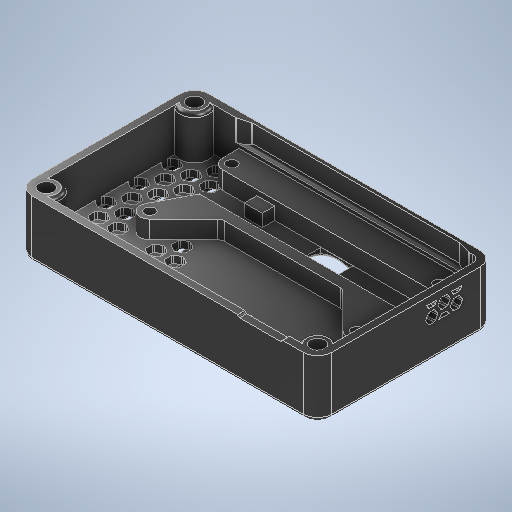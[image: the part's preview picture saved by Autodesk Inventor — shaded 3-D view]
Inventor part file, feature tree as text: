
AUTODESK INVENTOR PART (.ipt)
format: ipt  version: 2025 (Build 290162000, 162)  size: 2,251,264 bytes
history: native  units: mm
features: extrude x15, sketch x14, reference x9, fillet x8, projected_geometry x4, other x3, draft x1
ambient origin geometry x8: Origin, YZ Plane, XZ Plane, XY Plane, X Axis, Y Axis, Z Axis, Center Point
bodies: Solid1 (feature_tree)
feature tree (54):
  sketch  "Sketch1"  dims[d1=80.0mm d2=2.0mm]
  extrude  "Extrusion1"  Depth=2.0mm
  extrude  "Extrusion2"  Depth=5.5mm
  extrude  "Extrusion4"  Depth=9.1mm
  extrude  "Extrusion5"  Depth=2.0mm TaperAngle=0.0deg
  sketch  "Sketch2"  dims[d8=62.0mm d9=9.1mm]
  extrude  "Extrusion14"  Depth=12.0mm
  extrude  "Extrusion6"  Depth=5.0mm
  draft  "FaceDraft1"
  extrude  "Extrusion7"  Depth=13.0mm
  extrude  "Extrusion8"  Depth=4.0mm
  fillet  "Fillet6"  Radius=3.0mm
  fillet  "Fillet8"  Radius=2.0mm
  fillet  "Fillet9"  [1 undecoded]
  extrude  "Extrusion9"  Depth=5.0mm TaperAngle=0.0deg
  fillet  "Fillet10"  Radius=4.0mm
  extrude  "Extrusion11"  Depth=2.0mm
  fillet  "Fillet11"  Radius=2.0mm
  fillet  "Fillet12"  [1 undecoded]
  extrude  "Extrusion12"  Depth=2.0mm
  extrude  "Extrusion13"  TaperAngle=60.0deg  [1 undecoded]
  fillet  "Fillet13"  Radius=5.0mm
  extrude  "Extrusion15"  Depth=5.0mm
  fillet  "Fillet14"  Radius=7.0mm
  extrude  "Extrusion16"  Depth=8.0mm TaperAngle=0.0deg
  extrude  "Extrusion17"  Depth=0.5mm
  sketch  "Sketch Rectangular Pattern1"  dims[d3=2.0mm d4=2.9mm d5=58.0mm d6=23.0mm d7=5.5mm]
  projected_geometry  "Projected Loop2"
  sketch  "Sketch4"  dims[d10=9.0mm d11=2.0mm d12=0.0mm]
  sketch  "Sketch Rectangular Pattern6"  dims[d21=8.0mm d22=5.0mm]
  projected_geometry  "Projected Loop7"
  sketch  "Sketch5"  dims[d13=12.0mm d14=0.0mm d18=28.0mm]
  projected_geometry  "Projected Loop8"
  sketch  "Sketch Rectangular Pattern7"  dims[d32=2.0mm d33=4.0mm d34=3.0mm d35=2.0mm d36=135.0deg]
  sketch  "Sketch Rectangular Pattern8"  dims[d42=4.0mm d43=20.0mm d44=2.0mm d45=135.0deg]
  sketch  "Sketch Rectangular Pattern9"  dims[d51=2.0mm d52=0.0mm d54=60.0deg d55=5.0mm]
  sketch  "Sketch Rectangular Pattern10"  dims[d85=3.5mm d86=0.0mm d87=8.0mm d88=0.0mm d89=0.5mm d91=2.0mm d92=1.0mm d93=3.5mm d94=15.0mm d95=49.5mm d96=45.5mm d97=2.9mm d99=7.0mm d100=0.0mm d101=1.0mm d137=110.0mm d139=5.0mm d140=10.0mm d142=10.0mm d144=10.0mm d145=0.0mm d146=3.0mm d147=2.0mm d148=1.0mm d149=0.5mm d150=4.0mm d151=0.5mm d152=30.0mm d154=5.333333mm d155=10.0mm d157=10.0mm d159=40.0mm d161=5.333333mm d162=10.0mm d164=10.0mm d166=50.0mm d168=5.333333mm d169=10.0mm d171=10.0mm d173=90.0mm d175=5.333333mm d176=10.0mm d178=10.0mm d180=2.0mm d181=0.0mm d182=2.0mm d183=0.0mm d184=1.0mm d185=0.0mm d186=0.5mm d187=1.0mm d188=15.0deg d189=15.0deg d190=6.0mm d191=0.0mm d192=1.0mm d193=4.1mm d194=4.1mm d195=0.0mm d196=0.5mm d197=3.0mm d198=5.0mm d200=4.1mm d201=0.0mm d202=0.5mm d203=3.0mm d204=4.0mm d206=0.5mm d207=3.0mm d208=0.5mm d209=3.0mm d210=0.5mm d211=3.0mm d212=0.5mm d213=3.0mm d90=0.0mm]
  sketch  "Sketch6"  dims[d23=50.0mm d25=6.0mm d26=10.0mm d28=10.0mm d31=13.0mm]
  reference  "Reference1"
  reference  "Reference2"
  reference  "Reference3"
  reference  "Reference4"
  reference  "Reference5"
  reference  "Reference6"
  reference  "Reference7"
  reference  "Reference8"
  reference  "Reference9"
  sketch  "Sketch7"  dims[d37=135.0deg d38=5.0mm d39=0.0mm d40=4.0mm d41=0.0mm]
  projected_geometry  "Projected Loop9"
  sketch  "Sketch8"  dims[d46=135.0deg d50=2.0mm]
  sketch  "Sketch9"  dims[d82=3.5mm d83=5.0mm d84=7.0mm]
  parser-record x1  (decoder bookkeeping rows leaked as tree rows — omitted from the tree; the rows remain in map.json)
  other  "RemoteCameraModule.iam"
  other  "RemoteCasingBackCover:1"
note: 3 required parameter values undecoded (feature->parameter linkage not recoverable at this tier; creation-order binding heuristic only, values carry confidence <= 0.55)
note: 1 file-system path scrubbed to <path> (originals preserved in map.json)
